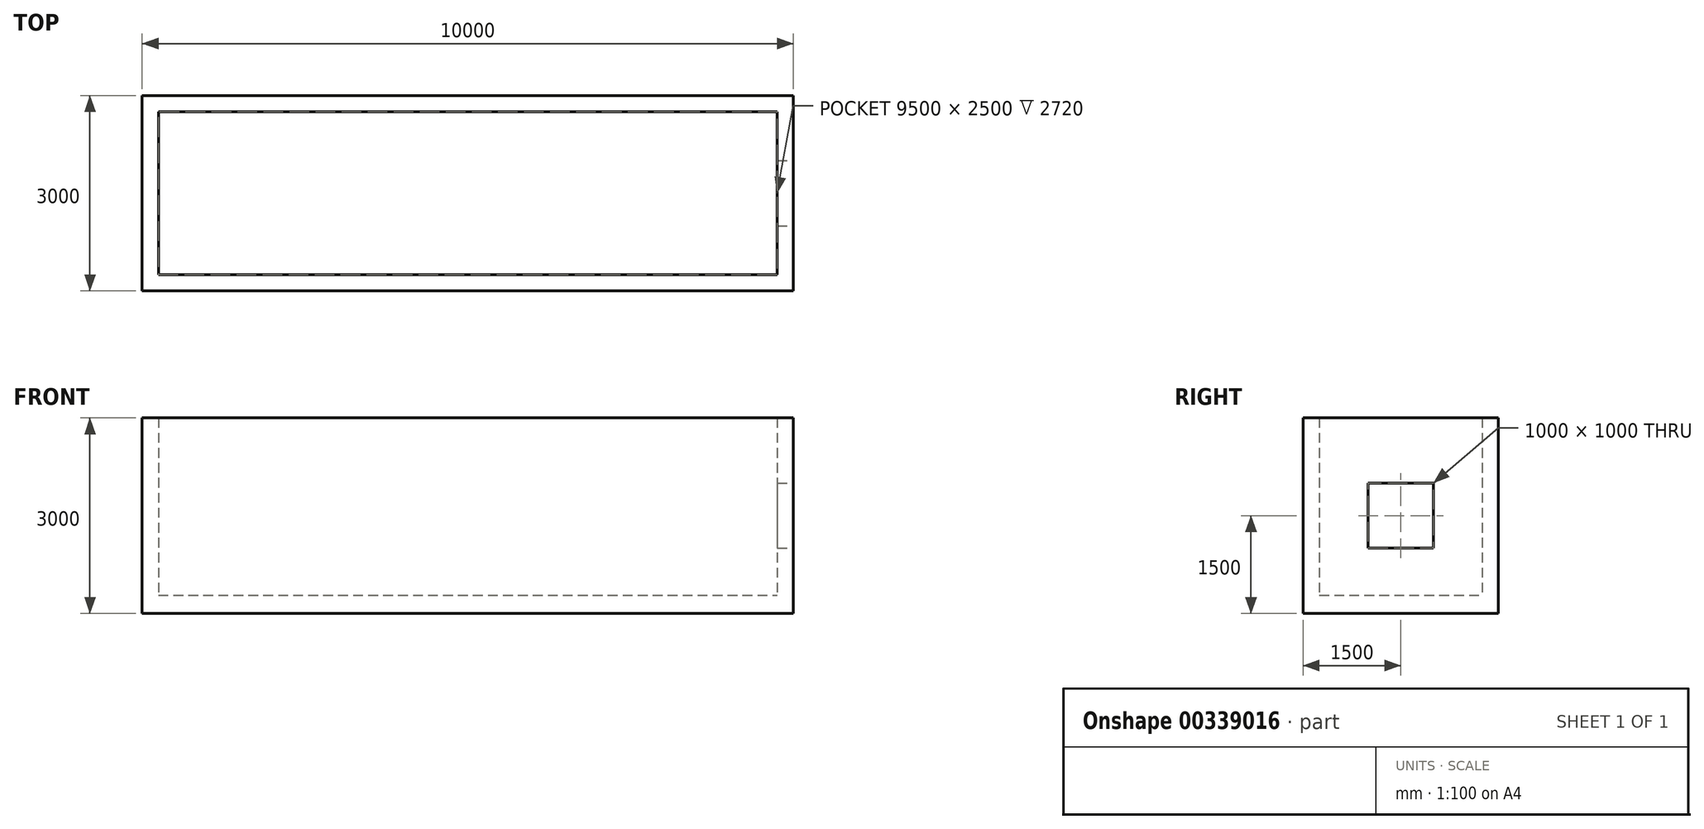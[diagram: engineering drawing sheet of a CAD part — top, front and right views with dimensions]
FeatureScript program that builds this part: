
annotation { "Feature Type Name" : "Feature", "Feature Type Description" : "" }
export const myFeature = defineFeature(function(context is Context, id is Id, definition is map)
    precondition{}
    {
        {
            var Q0;
            Q0=qCreatedBy(makeId("Top.planeOp"),FACE);
            var sketch = newSketch(context, id + "F0", { "sketchPlane" : qUnion([Q0])});
            skLineSegment(sketch, "E0.bottom", {"start": v(5000, 1500) * mm, "end": v(-5000, 1500) * mm});
            skLineSegment(sketch, "E0.top", {"start": v(5000, -1500) * mm, "end": v(-5000, -1500) * mm});
            skLineSegment(sketch, "E0.left", {"start": v(5000, 1500) * mm, "end": v(5000, -1500) * mm});
            skLineSegment(sketch, "E0.right", {"start": v(-5000, 1500) * mm, "end": v(-5000, -1500) * mm});
            skPoint(sketch, "E0.middle", {"position": v(0, 0) * mm});
            skSolve(sketch);
        }
        {
            var Q0;
            Q0 = qSketchRegion(id + "F0", true);
            extrude(context, id + "F1", {"entities" : qUnion([Q0]), "depth" : 280 * mm});
        }
        {
            var Q0;
            Q0=qCreatedBy(makeId("Top.planeOp"),FACE);
            var sketch = newSketch(context, id + "F2", { "sketchPlane" : qUnion([Q0])});
            skLineSegment(sketch, "E1.bottom", {"start": v(5000, -1500) * mm, "end": v(-5000, -1500) * mm});
            skLineSegment(sketch, "E1.top", {"start": v(5000, 1500) * mm, "end": v(-5000, 1500) * mm});
            skLineSegment(sketch, "E1.left", {"start": v(5000, -1500) * mm, "end": v(5000, 1500) * mm});
            skLineSegment(sketch, "E1.right", {"start": v(-5000, -1500) * mm, "end": v(-5000, 1500) * mm});
            skPoint(sketch, "E1.middle", {"position": v(0, 0) * mm});
            skLineSegment(sketch, "E2.bottom", {"start": v(4750, 1250) * mm, "end": v(-4750, 1250) * mm});
            skLineSegment(sketch, "E2.top", {"start": v(4750, -1250) * mm, "end": v(-4750, -1250) * mm});
            skLineSegment(sketch, "E2.left", {"start": v(4750, 1250) * mm, "end": v(4750, -1250) * mm});
            skLineSegment(sketch, "E2.right", {"start": v(-4750, 1250) * mm, "end": v(-4750, -1250) * mm});
            skSolve(sketch);
        }
        {
            var Q0;
            Q0 = qSketchRegion(id + "F2", true);
            extrude(context, id + "F3", {"entities" : qUnion([Q0]), "operationType" : NewBodyOperationType.ADD, "depth" : 3000 * mm});
        }
        {
            var Q0;
            Q0=makeQuery(id+"F3.boolean.opBoolean","MERGE",FACE,{"derivedFrom":[makeQuery(id+"F1.opExtrude","SWEPT_FACE",FACE,{"disambiguationData":[OSD([sQuery(id+"F0.wireOp",EDGE,"E0.left")])]}),makeQuery(id+"F3.opExtrude","SWEPT_FACE",FACE,{"disambiguationData":[OSD([sQuery(id+"F2.wireOp",EDGE,"E1.left")])]})]});
            var sketch = newSketch(context, id + "F4", { "sketchPlane" : qUnion([Q0])});
            skLineSegment(sketch, "E3.bottom", {"start": v(500, 2000) * mm, "end": v(-500, 2000) * mm});
            skLineSegment(sketch, "E3.top", {"start": v(500, 1000) * mm, "end": v(-500, 1000) * mm});
            skLineSegment(sketch, "E3.left", {"start": v(500, 2000) * mm, "end": v(500, 1000) * mm});
            skLineSegment(sketch, "E3.right", {"start": v(-500, 2000) * mm, "end": v(-500, 1000) * mm});
            skPoint(sketch, "E3.middle", {"position": v(0, 1500) * mm});
            skPoint(sketch, "E3.middle.positionSnap0", {"position": v(1500, 1500) * mm});
            skPoint(sketch, "E3.centerSnap0", {"position": v(1500, 1500) * mm});
            skSolve(sketch);
        }
        {
            var Q0;
            Q0 = qSketchRegion(id + "F4", true);
            extrude(context, id + "F5", {"entities" : qUnion([Q0]), "operationType" : NewBodyOperationType.REMOVE, "oppositeDirection" : true, "depth" : 1000 * mm});
        }
    });
